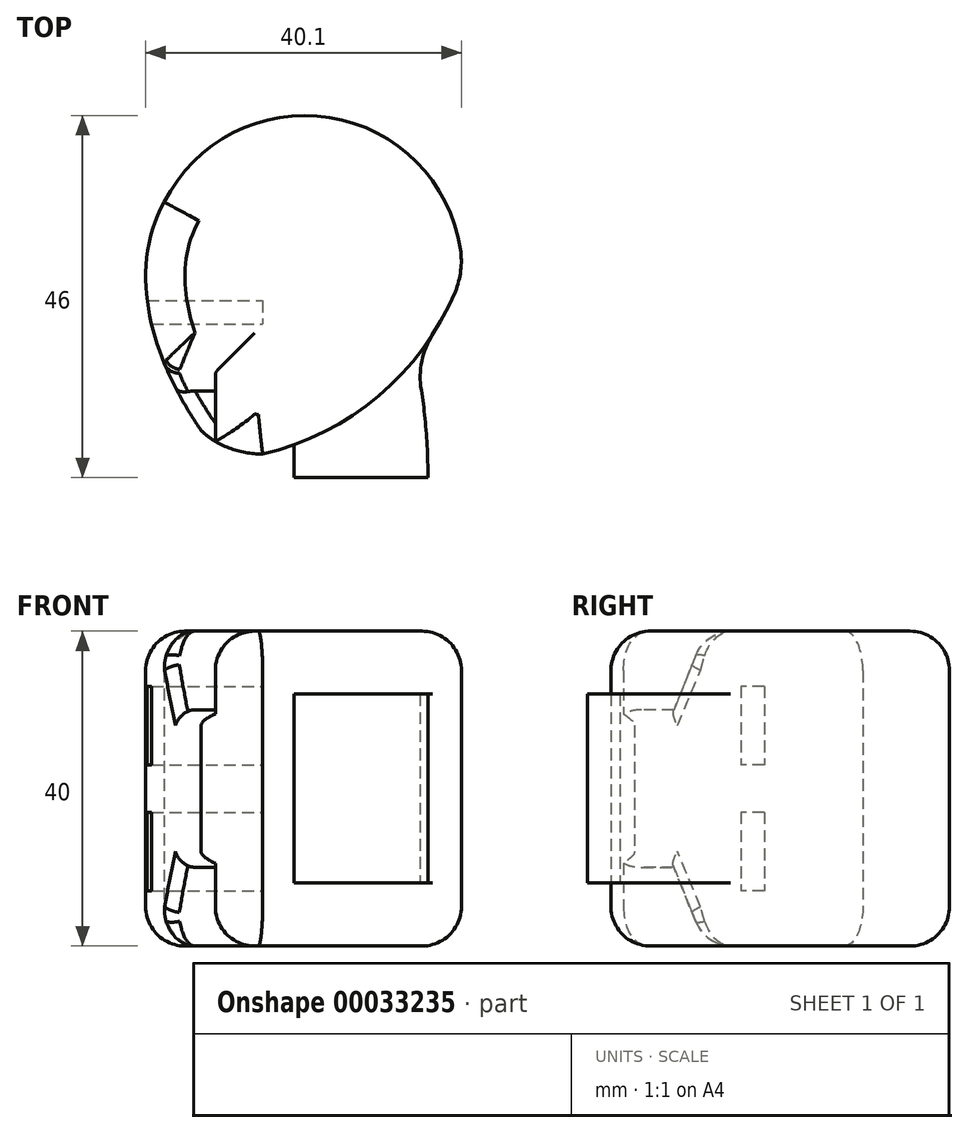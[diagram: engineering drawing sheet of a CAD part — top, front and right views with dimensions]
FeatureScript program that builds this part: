
annotation { "Feature Type Name" : "Feature", "Feature Type Description" : "" }
export const myFeature = defineFeature(function(context is Context, id is Id, definition is map)
    precondition{}
    {
        {
            var Q0;
            Q0=qCreatedBy(makeId("Top.planeOp"),FACE);
            var sketch = newSketch(context, id + "F0", { "sketchPlane" : qUnion([Q0])});
            skEllipticalArc(sketch, "E0", {});
            skLineSegment(sketch, "E1", {"start": v(-7.8, -5) * mm, "end": v(0, -5) * mm, "construction": true});
            skLineSegment(sketch, "E2", {"start": v(0, -5) * mm, "end": v(0, -8) * mm, "construction": true});
            skPoint(sketch, "E3.start.orphan", {"position": v(-10, 0) * mm});
            skEllipticalArc(sketch, "E4", {});
            skPoint(sketch, "E5", {"position": v(-12.5, 24) * mm});
            skEllipticalArc(sketch, "E6", {});
            skPoint(sketch, "E7", {"position": v(5.36, 35) * mm});
            skPoint(sketch, "E8", {"position": v(25.36, 15) * mm});
            skEllipticalArc(sketch, "E9.trimOffspring", {});
            skArc(sketch, "E10", {"start": v(0, -8) * mm, "mid": v(15.68, 0.19) * mm, "end": v(25.36, 15) * mm});
            const initialGuessF0  = {"E0": [0, 0, 0, 1, 0.008, 0.01, 2.245927859731882, 3.141592653589793], "E4": [0.03219375250200172, -0.001, -0.8727431764748058, 0.48817962669151427, 0.05121065819446363, 0.030073461642533206, 0, 0.8716590437257873], "E6": [0.005360571099491888, 0.015, 0, 1, 0.02, 0.02, 1.1040309877476178, 3.141592653589793], "E9.trimOffspring": [0.005360571099491888, 0.015, 0, 1, 0.02, 0.02, 4.71238898038469, 1.104030987747615]};
            skSetInitialGuess(sketch, initialGuessF0);
            skSolve(sketch);
        }
        {
            var Q0;
            Q0=qSketchRegion(id+"F0",true);
            extrude(context, id + "F1", {"entities" : qUnion([Q0]), "depth" : 20 * mm, "hasSecondDirection" : true, "secondDirectionOppositeDirection" : true, "secondDirectionDepth" : 20 * mm});
        }
        {
            var Q0;
            Q0=qCreatedBy(makeId("Right.planeOp"),FACE);
            var sketch = newSketch(context, id + "F2", { "sketchPlane" : qUnion([Q0])});
            skCircle(sketch, "E11", {"center": v(10, -8) * mm, "radius": 4 * mm, "construction": true});
            skLineSegment(sketch, "E12.bottom", {"start": v(11.5, -13) * mm, "end": v(8.5, -13) * mm});
            skLineSegment(sketch, "E12.top", {"start": v(11.5, -3) * mm, "end": v(8.5, -3) * mm});
            skLineSegment(sketch, "E12.left", {"start": v(11.5, -13) * mm, "end": v(11.5, -3) * mm});
            skLineSegment(sketch, "E12.right", {"start": v(8.5, -13) * mm, "end": v(8.5, -3) * mm});
            skPoint(sketch, "E13.MirrorP", {"position": v(10, 8) * mm});
            skLineSegment(sketch, "E14.MirrorCS", {"start": v(8.5, 13) * mm, "end": v(8.5, 3) * mm});
            skLineSegment(sketch, "E15.MirrorCS", {"start": v(11.5, 13) * mm, "end": v(11.5, 3) * mm});
            skLineSegment(sketch, "E16.MirrorCS", {"start": v(11.5, 3) * mm, "end": v(8.5, 3) * mm});
            skLineSegment(sketch, "E17.MirrorCS", {"start": v(11.5, 13) * mm, "end": v(8.5, 13) * mm});
            skSolve(sketch);
        }
        {
            var Q0;
            Q0=qSketchRegion(id+"F2",true);
            extrude(context, id + "F3", {"entities" : qUnion([Q0]), "operationType" : NewBodyOperationType.REMOVE, "endBound" : BoundingType.UP_TO_NEXT, "oppositeDirection" : true, "depth" : 25 * mm});
        }
        {
            var Q0;
            Q0=qCreatedBy(makeId("Top.planeOp"),FACE);
            var sketch = newSketch(context, id + "F4", { "sketchPlane" : qUnion([Q0])});
            skLineSegment(sketch, "E18", {"start": v(4, 0) * mm, "end": v(4, -11) * mm});
            skLineSegment(sketch, "E19", {"start": v(4, -11) * mm, "end": v(21, -11) * mm});
            skEllipticalArc(sketch, "E20", {});
            skPoint(sketch, "E21", {"position": v(16, 9) * mm});
            skLineSegment(sketch, "E22", {"start": v(16, 9) * mm, "end": v(4, 0) * mm});
            const initialGuessF4  = {"E20": [0.016, -0.011, 1, 0, 0.005, 0.02, 6.283185307179586, 1.5707963267948966]};
            skSetInitialGuess(sketch, initialGuessF4);
            skSolve(sketch);
        }
        {
            var Q0;
            Q0=qSketchRegion(id+"F4",true);
            extrude(context, id + "F5", {"entities" : qUnion([Q0]), "operationType" : NewBodyOperationType.ADD, "depth" : 12 * mm, "hasSecondDirection" : true, "secondDirectionOppositeDirection" : true, "secondDirectionDepth" : 12 * mm});
        }
        {
            var Q0;
            Q0=makeQuery(id+"F1.opExtrude","SWEPT_EDGE",EDGE,{"disambiguationData":[OSD([sQuery(id+"F0.wireOp",EDGE,"E9.trimOffspring"),sQuery(id+"F0.wireOp",EDGE,"E10")])]});
            var Q1;
            Q1=makeQuery(id+"F5.boolean.opBoolean","INTERSECT",EDGE,{"derivedFrom":[makeQuery(id+"F1.opExtrude","SWEPT_FACE",FACE,{"disambiguationData":[OSD([sQuery(id+"F0.wireOp",EDGE,"E10")])]}),makeQuery(id+"F5.opExtrude","SWEPT_FACE",FACE,{"disambiguationData":[OSD([sQuery(id+"F4.wireOp",EDGE,"E20")])]})]});
            fillet(context, id + "F6", {"entities" : qUnion([Q0, Q1]), "radius" : 10 * mm, "tangentPropagation" : true, "allowEdgeOverflow" : false});
        }
        {
            var Q0;
            Q0=qCreatedBy(makeId("Right.planeOp"),FACE);
            cPlane(context, id + "F7", {"entities" : qUnion([Q0]), "cplaneType" : CPlaneType.OFFSET, "offset" : 6 * mm, "oppositeDirection" : true, "width" : 150 * mm, "height" : 150 * mm});
        }
        {
            var Q0;
            Q0=qCreatedBy(id+"F7.planeOp",FACE);
            var sketch = newSketch(context, id + "F8", { "sketchPlane" : qUnion([Q0])});
            skLineSegment(sketch, "E23.0", {"start": v(24, -20) * mm, "end": v(-5, -20) * mm, "construction": true});
            skLineSegment(sketch, "E24.0", {"start": v(24, 20) * mm, "end": v(-5, 20) * mm, "construction": true});
            skLineSegment(sketch, "E25", {"start": v(4, -20) * mm, "end": v(0, -10) * mm});
            skLineSegment(sketch, "E26.0", {"start": v(-8, 20) * mm, "end": v(-8, -20) * mm, "construction": true});
            skLineSegment(sketch, "E27", {"start": v(0, -10) * mm, "end": v(-8, -10) * mm});
            skLineSegment(sketch, "E28", {"start": v(4, -20) * mm, "end": v(-8, -20) * mm});
            skLineSegment(sketch, "E29", {"start": v(-8, -10) * mm, "end": v(-8, -20) * mm});
            skLineSegment(sketch, "E30.MirrorCS", {"start": v(4, 20) * mm, "end": v(0, 10) * mm});
            skLineSegment(sketch, "E31.MirrorCS", {"start": v(0, 10) * mm, "end": v(-8, 10) * mm});
            skLineSegment(sketch, "E32.MirrorCS", {"start": v(4, 20) * mm, "end": v(-8, 20) * mm});
            skLineSegment(sketch, "E33", {"start": v(-8, 10) * mm, "end": v(-8, 20) * mm});
            skSolve(sketch);
        }
        {
            var Q0;
            Q0=qSketchRegion(id+"F8",true);
            extrude(context, id + "F9", {"entities" : qUnion([Q0]), "operationType" : NewBodyOperationType.REMOVE, "oppositeDirection" : true, "depth" : 25 * mm});
        }
        {
            var Q0;
            Q0=makeQuery(id+"F1.opExtrude","CAP_FACE",FACE,{"disambiguationData":[OSD([sQuery(id+"F0.wireOp",EDGE,"E0"),sQuery(id+"F0.wireOp",EDGE,"E4"),sQuery(id+"F0.wireOp",EDGE,"E9.trimOffspring"),sQuery(id+"F0.wireOp",EDGE,"E10")])],"isStart":true});
            var Q1;
            Q1=makeQuery(id+"F1.opExtrude","CAP_FACE",FACE,{"disambiguationData":[OSD([sQuery(id+"F0.wireOp",EDGE,"E0"),sQuery(id+"F0.wireOp",EDGE,"E4"),sQuery(id+"F0.wireOp",EDGE,"E9.trimOffspring"),sQuery(id+"F0.wireOp",EDGE,"E10")])],"isStart":false});
            fillet(context, id + "F10", {"entities" : qUnion([Q0, Q1]), "radius" : 5 * mm, "tangentPropagation" : true, "allowEdgeOverflow" : false});
        }
        {
            var Q0;
            Q0=makeQuery(id+"F9.boolean.opBoolean","INTERSECT",EDGE,{"derivedFrom":[makeQuery(id+"F1.opExtrude","SWEPT_FACE",FACE,{"disambiguationData":[OSD([sQuery(id+"F0.wireOp",EDGE,"E4")])]}),makeQuery(id+"F9.opExtrude","SWEPT_FACE",FACE,{"disambiguationData":[OSD([sQuery(id+"F8.wireOp",EDGE,"E27")])]})]});
            var Q1;
            Q1=makeQuery(id+"F9.boolean.opBoolean","INTERSECT",EDGE,{"derivedFrom":[makeQuery(id+"F1.opExtrude","SWEPT_FACE",FACE,{"disambiguationData":[OSD([sQuery(id+"F0.wireOp",EDGE,"E4")])]}),makeQuery(id+"F9.opExtrude","SWEPT_FACE",FACE,{"disambiguationData":[OSD([sQuery(id+"F8.wireOp",EDGE,"E31.MirrorCS")])]})]});
            var Q2;
            Q2=makeQuery(id+"F9.boolean.opBoolean","INTERSECT",EDGE,{"derivedFrom":[makeQuery(id+"F1.opExtrude","SWEPT_FACE",FACE,{"disambiguationData":[OSD([sQuery(id+"F0.wireOp",EDGE,"E4")])]}),makeQuery(id+"F9.opExtrude","SWEPT_FACE",FACE,{"disambiguationData":[OSD([sQuery(id+"F8.wireOp",EDGE,"E25")])]})]});
            var Q3;
            Q3=makeQuery(id+"F9.boolean.opBoolean","INTERSECT",EDGE,{"derivedFrom":[makeQuery(id+"F1.opExtrude","SWEPT_FACE",FACE,{"disambiguationData":[OSD([sQuery(id+"F0.wireOp",EDGE,"E4")])]}),makeQuery(id+"F9.opExtrude","SWEPT_FACE",FACE,{"disambiguationData":[OSD([sQuery(id+"F8.wireOp",EDGE,"E30.MirrorCS")])]})]});
            fillet(context, id + "F11", {"entities" : qUnion([Q0, Q1, Q2, Q3]), "radius" : 2 * mm, "tangentPropagation" : true, "allowEdgeOverflow" : false});
        }
    });
